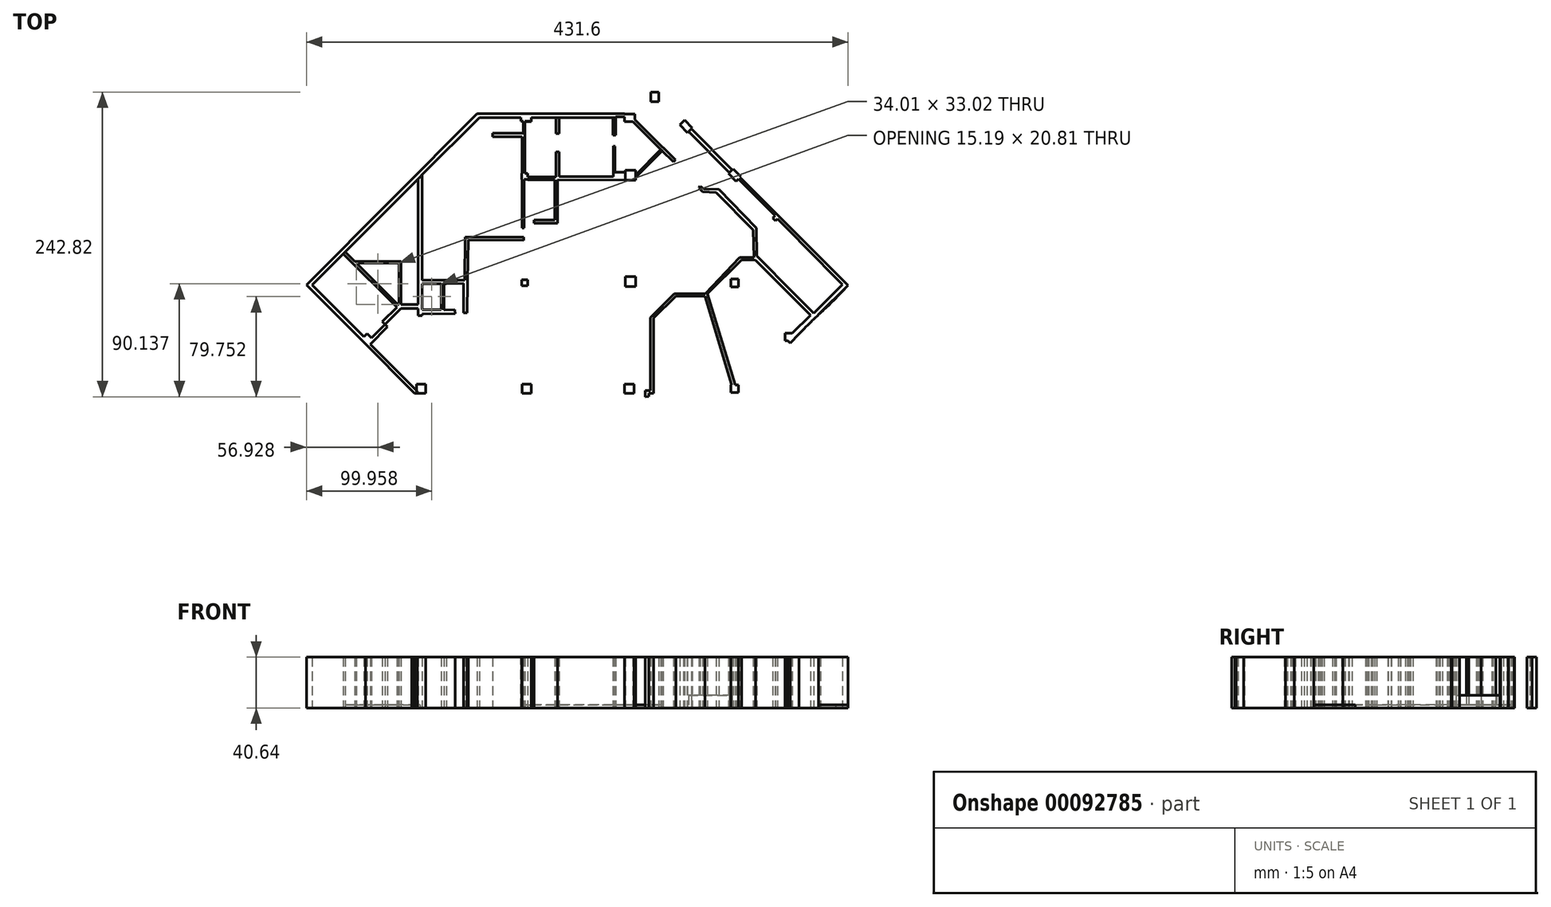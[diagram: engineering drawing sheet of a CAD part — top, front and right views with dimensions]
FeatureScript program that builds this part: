
annotation { "Feature Type Name" : "Feature", "Feature Type Description" : "" }
export const myFeature = defineFeature(function(context is Context, id is Id, definition is map)
    precondition{}
    {
        {
            var Q0;
            Q0=qCreatedBy(makeId("Top.planeOp"),FACE);
            var sketch = newSketch(context, id + "F0", { "sketchPlane" : qUnion([Q0])});
            skFitSpline(sketch, "E0", {"points": [v(215.85, -30.91) * mm, v(202.31, -44.9) * mm, v(186.07, -60.28) * mm, v(172.5, -74.45) * mm]});
            skFitSpline(sketch, "E1", {"points": [v(172.5, -74.45) * mm, v(171.88, -75.1) * mm, v(175.67, -77.18) * mm, v(175.03, -77.82) * mm]});
            skLineSegment(sketch, "E2", {"start": v(-215.85, -30.42) * mm, "end": v(-79.78, 105.85) * mm});
            skLineSegment(sketch, "E3", {"start": v(-79.78, 105.85) * mm, "end": v(46.96, 105.85) * mm});
            skLineSegment(sketch, "E4", {"start": v(46.96, 105.85) * mm, "end": v(58.85, 117.75) * mm});
            skLineSegment(sketch, "E5", {"start": v(58.85, 117.75) * mm, "end": v(58.85, 123.23) * mm});
            skLineSegment(sketch, "E6", {"start": v(58.85, 123.23) * mm, "end": v(65.02, 123.23) * mm});
            skLineSegment(sketch, "E7", {"start": v(65.02, 123.23) * mm, "end": v(65.02, 119.77) * mm});
            skLineSegment(sketch, "E8", {"start": v(65.02, 119.77) * mm, "end": v(84.8, 100) * mm});
            skLineSegment(sketch, "E9", {"start": v(84.8, 100) * mm, "end": v(85.59, 100.78) * mm});
            skLineSegment(sketch, "E10", {"start": v(85.59, 100.78) * mm, "end": v(91.7, 94.67) * mm});
            skLineSegment(sketch, "E11", {"start": v(91.7, 94.67) * mm, "end": v(90.95, 93.92) * mm});
            skLineSegment(sketch, "E12", {"start": v(90.95, 93.92) * mm, "end": v(123.63, 61.24) * mm});
            skLineSegment(sketch, "E13", {"start": v(123.63, 61.24) * mm, "end": v(124.34, 61.95) * mm});
            skLineSegment(sketch, "E14", {"start": v(124.34, 61.95) * mm, "end": v(130.43, 55.86) * mm});
            skLineSegment(sketch, "E15", {"start": v(130.43, 55.86) * mm, "end": v(129.76, 55.18) * mm});
            skLineSegment(sketch, "E16", {"start": v(129.76, 55.18) * mm, "end": v(215.85, -30.91) * mm});
            skLineSegment(sketch, "E17", {"start": v(175.03, -77.82) * mm, "end": v(130.22, -123.23) * mm});
            skLineSegment(sketch, "E18", {"start": v(130.22, -123.23) * mm, "end": v(-126.45, -123.2) * mm});
            skLineSegment(sketch, "E19", {"start": v(-126.45, -123.2) * mm, "end": v(-126.52, -117) * mm});
            skLineSegment(sketch, "E20", {"start": v(-126.52, -117) * mm, "end": v(-129.44, -116.92) * mm});
            skLineSegment(sketch, "E21", {"start": v(-129.44, -116.92) * mm, "end": v(-132.8, -113.69) * mm});
            skLineSegment(sketch, "E22", {"start": v(-132.8, -113.69) * mm, "end": v(-167.08, -79.4) * mm});
            skLineSegment(sketch, "E23", {"start": v(-167.08, -79.4) * mm, "end": v(-168.6, -77.64) * mm});
            skLineSegment(sketch, "E24", {"start": v(-168.6, -77.64) * mm, "end": v(-215.85, -30.42) * mm});
            skLineSegment(sketch, "E25", {"start": v(-126.82, 53.9) * mm, "end": v(-126.8, -46) * mm});
            skLineSegment(sketch, "E26", {"start": v(-126.8, -46) * mm, "end": v(-140.51, -46) * mm});
            skLineSegment(sketch, "E27", {"start": v(-140.51, -46) * mm, "end": v(-140.51, -11.77) * mm});
            skLineSegment(sketch, "E28", {"start": v(-140.51, -11.77) * mm, "end": v(-177.03, -11.77) * mm});
            skLineSegment(sketch, "E29", {"start": v(-177.03, -11.77) * mm, "end": v(-184.78, -4.06) * mm});
            skLineSegment(sketch, "E30", {"start": v(-184.78, -4.06) * mm, "end": v(-186.43, -5.7) * mm});
            skLineSegment(sketch, "E31", {"start": v(-186.43, -5.7) * mm, "end": v(-143.7, -48.36) * mm});
            skLineSegment(sketch, "E32", {"start": v(-143.7, -48.36) * mm, "end": v(-155.43, -59.75) * mm});
            skLineSegment(sketch, "E33", {"start": v(-155.43, -59.75) * mm, "end": v(-153.01, -61.89) * mm});
            skLineSegment(sketch, "E34", {"start": v(-153.01, -61.89) * mm, "end": v(-140.38, -49.21) * mm});
            skLineSegment(sketch, "E35", {"start": v(-140.38, -49.21) * mm, "end": v(-126.8, -49.28) * mm});
            skLineSegment(sketch, "E36", {"start": v(-126.8, -49.28) * mm, "end": v(-126.8, -55.02) * mm});
            skLineSegment(sketch, "E37", {"start": v(-126.8, -55.02) * mm, "end": v(-123.39, -55.02) * mm});
            skLineSegment(sketch, "E38", {"start": v(-123.39, -55.02) * mm, "end": v(-123.39, -53.84) * mm});
            skLineSegment(sketch, "E39", {"start": v(-123.39, -53.84) * mm, "end": v(-97.3, -53.56) * mm});
            skLineSegment(sketch, "E40", {"start": v(-97.3, -53.56) * mm, "end": v(-97.4, -50.34) * mm});
            skLineSegment(sketch, "E41", {"start": v(-97.4, -50.34) * mm, "end": v(-106.13, -50.62) * mm});
            skLineSegment(sketch, "E42", {"start": v(-106.13, -50.62) * mm, "end": v(-106.13, -47.71) * mm});
            skLineSegment(sketch, "E43", {"start": v(-106.13, -47.71) * mm, "end": v(-106.13, -37.32) * mm});
            skLineSegment(sketch, "E44", {"start": v(-106.13, -37.32) * mm, "end": v(-106.13, -29.47) * mm});
            skLineSegment(sketch, "E45", {"start": v(-106.13, -29.47) * mm, "end": v(-104.14, -29.47) * mm});
            skLineSegment(sketch, "E46", {"start": v(-104.14, -29.47) * mm, "end": v(-90.55, -29.32) * mm});
            skLineSegment(sketch, "E47", {"start": v(-90.55, -29.32) * mm, "end": v(-90.46, -52.83) * mm});
            skLineSegment(sketch, "E48", {"start": v(-90.46, -52.83) * mm, "end": v(-87.5, -52.8) * mm});
            skLineSegment(sketch, "E49", {"start": v(-87.5, -52.8) * mm, "end": v(-87.23, -27.68) * mm});
            skLineSegment(sketch, "E50", {"start": v(-87.23, -27.68) * mm, "end": v(-86.84, 5.2) * mm});
            skLineSegment(sketch, "E51", {"start": v(-86.84, 5.2) * mm, "end": v(-42.6, 4.94) * mm});
            skLineSegment(sketch, "E52", {"start": v(-42.6, 4.94) * mm, "end": v(-42.48, 7.54) * mm});
            skLineSegment(sketch, "E53", {"start": v(-42.48, 7.54) * mm, "end": v(-89.25, 7.47) * mm});
            skLineSegment(sketch, "E54", {"start": v(-89.25, 7.47) * mm, "end": v(-89.44, -26.72) * mm});
            skLineSegment(sketch, "E55", {"start": v(-89.44, -26.72) * mm, "end": v(-100.11, -26.77) * mm});
            skLineSegment(sketch, "E56", {"start": v(-100.11, -26.77) * mm, "end": v(-103.15, -26.77) * mm});
            skLineSegment(sketch, "E57", {"start": v(-103.15, -26.77) * mm, "end": v(-123.39, -26.77) * mm});
            skLineSegment(sketch, "E58", {"start": v(-123.39, -26.77) * mm, "end": v(-123.39, 24.46) * mm});
            skLineSegment(sketch, "E59", {"start": v(-123.39, 24.46) * mm, "end": v(-123.4, 57.33) * mm});
            skLineSegment(sketch, "E60", {"start": v(-123.4, 57.33) * mm, "end": v(-126.82, 53.9) * mm});
            skLineSegment(sketch, "E61", {"start": v(-16.97, 102.82) * mm, "end": v(-16.98, 90.17) * mm});
            skLineSegment(sketch, "E62", {"start": v(-16.98, 90.17) * mm, "end": v(-14.46, 90.17) * mm});
            skLineSegment(sketch, "E63", {"start": v(-14.46, 90.17) * mm, "end": v(-14.46, 102.82) * mm});
            skLineSegment(sketch, "E64", {"start": v(-14.46, 102.82) * mm, "end": v(-16.97, 102.82) * mm});
            skFitSpline(sketch, "E65", {"points": [v(-43.9, 14.88) * mm, v(-43.9, 14.88) * mm, v(-42.18, 14.58) * mm, v(-42.18, 14.88) * mm, v(-43.9, 14.88) * mm]});
            skLineSegment(sketch, "E66", {"start": v(66.76, 77.4) * mm, "end": v(46.57, 57.21) * mm});
            skLineSegment(sketch, "E67", {"start": v(46.57, 57.21) * mm, "end": v(46.57, 56.84) * mm});
            skLineSegment(sketch, "E68", {"start": v(46.57, 56.84) * mm, "end": v(46.57, 60.9) * mm});
            skLineSegment(sketch, "E69", {"start": v(46.57, 60.9) * mm, "end": v(38.5, 60.9) * mm});
            skLineSegment(sketch, "E70", {"start": v(38.5, 60.9) * mm, "end": v(38.5, 59.43) * mm});
            skLineSegment(sketch, "E71", {"start": v(38.5, 59.43) * mm, "end": v(30.24, 59.43) * mm});
            skLineSegment(sketch, "E72", {"start": v(30.24, 59.43) * mm, "end": v(30.24, 79.9) * mm});
            skLineSegment(sketch, "E73", {"start": v(30.24, 79.9) * mm, "end": v(28.78, 80.3) * mm});
            skLineSegment(sketch, "E74", {"start": v(28.78, 80.3) * mm, "end": v(28.78, 55.7) * mm});
            skLineSegment(sketch, "E75", {"start": v(28.78, 55.7) * mm, "end": v(27.67, 55.7) * mm});
            skLineSegment(sketch, "E76", {"start": v(27.67, 55.7) * mm, "end": v(-14.36, 55.7) * mm});
            skLineSegment(sketch, "E77", {"start": v(-14.36, 55.7) * mm, "end": v(-14.36, 75.35) * mm});
            skLineSegment(sketch, "E78", {"start": v(-14.36, 75.35) * mm, "end": v(-16.88, 75.35) * mm});
            skLineSegment(sketch, "E79", {"start": v(-16.88, 75.35) * mm, "end": v(-16.88, 55.6) * mm});
            skLineSegment(sketch, "E80", {"start": v(-16.88, 55.6) * mm, "end": v(-39.28, 55.6) * mm});
            skLineSegment(sketch, "E81", {"start": v(-39.28, 55.6) * mm, "end": v(-39.28, 58.34) * mm});
            skLineSegment(sketch, "E82", {"start": v(-39.28, 58.34) * mm, "end": v(-41.58, 58.34) * mm});
            skLineSegment(sketch, "E83", {"start": v(-41.58, 58.34) * mm, "end": v(-41.58, 99.68) * mm});
            skLineSegment(sketch, "E84", {"start": v(-41.58, 99.68) * mm, "end": v(-36.58, 99.68) * mm});
            skLineSegment(sketch, "E85", {"start": v(-36.58, 99.68) * mm, "end": v(-36.58, 102.83) * mm});
            skLineSegment(sketch, "E86", {"start": v(-36.58, 102.83) * mm, "end": v(-44.9, 102.83) * mm});
            skLineSegment(sketch, "E87", {"start": v(-44.9, 102.83) * mm, "end": v(-44.98, 99.68) * mm});
            skLineSegment(sketch, "E88", {"start": v(-44.98, 99.68) * mm, "end": v(-42.68, 99.68) * mm});
            skLineSegment(sketch, "E89", {"start": v(-42.68, 99.68) * mm, "end": v(-42.68, 90.28) * mm});
            skLineSegment(sketch, "E90", {"start": v(-42.68, 90.28) * mm, "end": v(-67.28, 90.28) * mm});
            skLineSegment(sketch, "E91", {"start": v(-67.28, 90.28) * mm, "end": v(-67.28, 87.66) * mm});
            skLineSegment(sketch, "E92", {"start": v(-67.28, 87.66) * mm, "end": v(-43.8, 87.66) * mm});
            skLineSegment(sketch, "E93", {"start": v(-43.8, 87.66) * mm, "end": v(-43.8, 58.34) * mm});
            skLineSegment(sketch, "E94", {"start": v(-43.8, 58.34) * mm, "end": v(-44.13, 58.34) * mm});
            skLineSegment(sketch, "E95", {"start": v(-44.13, 58.34) * mm, "end": v(-44.13, 53.49) * mm});
            skLineSegment(sketch, "E96", {"start": v(-44.13, 53.49) * mm, "end": v(-43.9, 53.49) * mm});
            skLineSegment(sketch, "E97", {"start": v(-43.9, 53.49) * mm, "end": v(-43.9, 14.88) * mm});
            skFitSpline(sketch, "E98", {"points": [v(46.56, 55.03) * mm, v(47.71, 55.85) * mm, v(67.81, 76.29) * mm, v(67.81, 76.29) * mm, v(46.56, 55.03) * mm]});
            skLineSegment(sketch, "E99", {"start": v(-42.18, 14.88) * mm, "end": v(-42.18, 53.49) * mm});
            skLineSegment(sketch, "E100", {"start": v(-42.18, 53.49) * mm, "end": v(-39.46, 53.49) * mm});
            skLineSegment(sketch, "E101", {"start": v(-39.46, 53.49) * mm, "end": v(-39.46, 53.29) * mm});
            skLineSegment(sketch, "E102", {"start": v(-39.46, 53.29) * mm, "end": v(-17.89, 53.29) * mm});
            skLineSegment(sketch, "E103", {"start": v(-17.89, 53.29) * mm, "end": v(-17.89, 21.13) * mm});
            skLineSegment(sketch, "E104", {"start": v(-17.89, 21.13) * mm, "end": v(-34.32, 21.13) * mm});
            skLineSegment(sketch, "E105", {"start": v(-34.32, 21.13) * mm, "end": v(-34.32, 18.81) * mm});
            skLineSegment(sketch, "E106", {"start": v(-34.32, 18.81) * mm, "end": v(-15.67, 18.81) * mm});
            skLineSegment(sketch, "E107", {"start": v(-15.67, 18.81) * mm, "end": v(-15.67, 53.08) * mm});
            skLineSegment(sketch, "E108", {"start": v(-15.67, 53.08) * mm, "end": v(38.5, 53.08) * mm});
            skLineSegment(sketch, "E109", {"start": v(38.5, 53.08) * mm, "end": v(38.5, 52.83) * mm});
            skLineSegment(sketch, "E110", {"start": v(38.5, 52.83) * mm, "end": v(46.56, 52.83) * mm});
            skLineSegment(sketch, "E111", {"start": v(46.56, 52.83) * mm, "end": v(46.56, 55.03) * mm});
            skLineSegment(sketch, "E112", {"start": v(67.81, 76.29) * mm, "end": v(66.76, 77.4) * mm});
            skLineSegment(sketch, "E113", {"start": v(76.66, 67.44) * mm, "end": v(78.4, 69.18) * mm});
            skLineSegment(sketch, "E114", {"start": v(78.4, 69.18) * mm, "end": v(68.46, 79.11) * mm});
            skLineSegment(sketch, "E115", {"start": v(68.46, 79.11) * mm, "end": v(68.37, 79.01) * mm});
            skLineSegment(sketch, "E116", {"start": v(68.37, 79.01) * mm, "end": v(46.1, 101.07) * mm});
            skLineSegment(sketch, "E117", {"start": v(46.1, 101.07) * mm, "end": v(46.1, 105.52) * mm});
            skLineSegment(sketch, "E118", {"start": v(46.1, 105.52) * mm, "end": v(37.73, 105.52) * mm});
            skLineSegment(sketch, "E119", {"start": v(37.73, 105.52) * mm, "end": v(37.7, 105.8) * mm});
            skLineSegment(sketch, "E120", {"start": v(37.7, 105.8) * mm, "end": v(-79.76, 105.8) * mm});
            skLineSegment(sketch, "E121", {"start": v(-79.76, 105.8) * mm, "end": v(-215.75, -30.47) * mm});
            skLineSegment(sketch, "E122", {"start": v(-215.75, -30.47) * mm, "end": v(-168.57, -77.66) * mm});
            skLineSegment(sketch, "E123", {"start": v(-168.57, -77.66) * mm, "end": v(-168.48, -77.57) * mm});
            skLineSegment(sketch, "E124", {"start": v(-168.48, -77.57) * mm, "end": v(-129.43, -117.04) * mm});
            skLineSegment(sketch, "E125", {"start": v(-129.43, -117.04) * mm, "end": v(-127.3, -117.04) * mm});
            skLineSegment(sketch, "E126", {"start": v(-127.3, -117.04) * mm, "end": v(-127.3, -115.33) * mm});
            skLineSegment(sketch, "E127", {"start": v(-127.3, -115.33) * mm, "end": v(-164.85, -77.78) * mm});
            skLineSegment(sketch, "E128", {"start": v(-164.85, -77.78) * mm, "end": v(-151.03, -63.95) * mm});
            skLineSegment(sketch, "E129", {"start": v(-151.03, -63.95) * mm, "end": v(-153.09, -61.88) * mm});
            skLineSegment(sketch, "E130", {"start": v(-153.09, -61.88) * mm, "end": v(-163.87, -72.66) * mm});
            skLineSegment(sketch, "E131", {"start": v(-163.87, -72.66) * mm, "end": v(-167.29, -69.24) * mm});
            skLineSegment(sketch, "E132", {"start": v(-167.29, -69.24) * mm, "end": v(-169.86, -71.8) * mm});
            skLineSegment(sketch, "E133", {"start": v(-169.86, -71.8) * mm, "end": v(-211.2, -30.47) * mm});
            skLineSegment(sketch, "E134", {"start": v(-211.2, -30.47) * mm, "end": v(-77.91, 102.8) * mm});
            skLineSegment(sketch, "E135", {"start": v(-77.91, 102.8) * mm, "end": v(-56.96, 102.8) * mm});
            skLineSegment(sketch, "E136", {"start": v(-56.96, 102.8) * mm, "end": v(-53.35, 102.8) * mm});
            skLineSegment(sketch, "E137", {"start": v(-53.35, 102.8) * mm, "end": v(28.56, 102.8) * mm});
            skLineSegment(sketch, "E138", {"start": v(28.56, 102.8) * mm, "end": v(30.9, 102.84) * mm});
            skLineSegment(sketch, "E139", {"start": v(30.9, 102.84) * mm, "end": v(30.91, 103.52) * mm});
            skLineSegment(sketch, "E140", {"start": v(30.91, 103.52) * mm, "end": v(37.7, 103.52) * mm});
            skLineSegment(sketch, "E141", {"start": v(37.7, 103.52) * mm, "end": v(37.7, 99.68) * mm});
            skLineSegment(sketch, "E142", {"start": v(37.7, 99.68) * mm, "end": v(44.47, 99.68) * mm});
            skLineSegment(sketch, "E143", {"start": v(44.47, 99.68) * mm, "end": v(76.66, 67.44) * mm});
            skLineSegment(sketch, "E144", {"start": v(28.57, 102.8) * mm, "end": v(28.56, 88.7) * mm});
            skLineSegment(sketch, "E145", {"start": v(28.56, 88.7) * mm, "end": v(30.91, 88.76) * mm});
            skLineSegment(sketch, "E146", {"start": v(30.91, 88.76) * mm, "end": v(30.88, 102.86) * mm});
            skLineSegment(sketch, "E147", {"start": v(30.88, 102.86) * mm, "end": v(28.57, 102.8) * mm});
            skLineSegment(sketch, "E148", {"start": v(-175.83, -12.98) * mm, "end": v(-141.82, -12.98) * mm});
            skLineSegment(sketch, "E149", {"start": v(-141.82, -12.98) * mm, "end": v(-141.82, -46) * mm});
            skLineSegment(sketch, "E150", {"start": v(-141.82, -46) * mm, "end": v(-142.77, -46) * mm});
            skLineSegment(sketch, "E151", {"start": v(-142.77, -46) * mm, "end": v(-175.83, -12.98) * mm});
            skLineSegment(sketch, "E152", {"start": v(-123.39, -29.47) * mm, "end": v(-108.2, -29.47) * mm});
            skLineSegment(sketch, "E153", {"start": v(-108.2, -29.47) * mm, "end": v(-108.2, -36.4) * mm});
            skLineSegment(sketch, "E154", {"start": v(-108.2, -36.4) * mm, "end": v(-108.41, -47.51) * mm});
            skLineSegment(sketch, "E155", {"start": v(-108.41, -47.51) * mm, "end": v(-108.38, -50.28) * mm});
            skLineSegment(sketch, "E156", {"start": v(-108.38, -50.28) * mm, "end": v(-123.39, -50.28) * mm});
            skLineSegment(sketch, "E157", {"start": v(-123.39, -50.28) * mm, "end": v(-123.39, -29.47) * mm});
            skLineSegment(sketch, "E158", {"start": v(-44.13, -26.48) * mm, "end": v(-39.28, -26.48) * mm});
            skLineSegment(sketch, "E159", {"start": v(-39.28, -26.48) * mm, "end": v(-39.28, -31.32) * mm});
            skLineSegment(sketch, "E160", {"start": v(-39.28, -31.32) * mm, "end": v(-44.13, -31.32) * mm});
            skLineSegment(sketch, "E161", {"start": v(-44.13, -31.32) * mm, "end": v(-44.13, -26.48) * mm});
            skLineSegment(sketch, "E162", {"start": v(124.35, 62) * mm, "end": v(120.57, 58.23) * mm});
            skLineSegment(sketch, "E163", {"start": v(120.57, 58.23) * mm, "end": v(126.7, 52.1) * mm});
            skLineSegment(sketch, "E164", {"start": v(126.7, 52.1) * mm, "end": v(128.56, 53.96) * mm});
            skLineSegment(sketch, "E165", {"start": v(128.56, 53.96) * mm, "end": v(157.7, 24.77) * mm});
            skLineSegment(sketch, "E166", {"start": v(157.7, 24.77) * mm, "end": v(155.8, 22.87) * mm});
            skLineSegment(sketch, "E167", {"start": v(155.8, 22.87) * mm, "end": v(157.96, 20.48) * mm});
            skLineSegment(sketch, "E168", {"start": v(157.96, 20.48) * mm, "end": v(159.59, 22.13) * mm});
            skLineSegment(sketch, "E169", {"start": v(159.59, 22.13) * mm, "end": v(193.9, -12.57) * mm});
            skLineSegment(sketch, "E170", {"start": v(193.9, -12.57) * mm, "end": v(198.22, -16.85) * mm});
            skLineSegment(sketch, "E171", {"start": v(198.22, -16.85) * mm, "end": v(211.45, -30.18) * mm});
            skLineSegment(sketch, "E172", {"start": v(211.45, -30.18) * mm, "end": v(188.53, -53.1) * mm});
            skLineSegment(sketch, "E173", {"start": v(188.53, -53.1) * mm, "end": v(172.67, -37.2) * mm});
            skLineSegment(sketch, "E174", {"start": v(172.67, -37.2) * mm, "end": v(143.11, -7.23) * mm});
            skLineSegment(sketch, "E175", {"start": v(143.11, -7.23) * mm, "end": v(142.78, 14.73) * mm});
            skLineSegment(sketch, "E176", {"start": v(142.78, 14.73) * mm, "end": v(113, 45.5) * mm});
            skLineSegment(sketch, "E177", {"start": v(113, 45.5) * mm, "end": v(100.86, 45.83) * mm});
            skLineSegment(sketch, "E178", {"start": v(100.86, 45.83) * mm, "end": v(98.06, 48.17) * mm});
            skLineSegment(sketch, "E179", {"start": v(98.06, 48.17) * mm, "end": v(97.12, 46.46) * mm});
            skLineSegment(sketch, "E180", {"start": v(97.12, 46.46) * mm, "end": v(99.87, 43.74) * mm});
            skLineSegment(sketch, "E181", {"start": v(99.87, 43.74) * mm, "end": v(110.89, 43.22) * mm});
            skLineSegment(sketch, "E182", {"start": v(110.89, 43.22) * mm, "end": v(140.17, 13.18) * mm});
            skLineSegment(sketch, "E183", {"start": v(140.17, 13.18) * mm, "end": v(141.01, -8.52) * mm});
            skLineSegment(sketch, "E184", {"start": v(141.01, -8.52) * mm, "end": v(129.6, -8.57) * mm});
            skLineSegment(sketch, "E185", {"start": v(129.6, -8.57) * mm, "end": v(102.25, -37.52) * mm});
            skLineSegment(sketch, "E186", {"start": v(102.25, -37.52) * mm, "end": v(87.7, -37.53) * mm});
            skLineSegment(sketch, "E187", {"start": v(87.7, -37.53) * mm, "end": v(87.7, -37.54) * mm});
            skLineSegment(sketch, "E188", {"start": v(87.7, -37.54) * mm, "end": v(77.36, -37.54) * mm});
            skLineSegment(sketch, "E189", {"start": v(77.36, -37.54) * mm, "end": v(58.26, -56.63) * mm});
            skLineSegment(sketch, "E190", {"start": v(58.26, -56.63) * mm, "end": v(58.26, -114.64) * mm});
            skLineSegment(sketch, "E191", {"start": v(58.26, -114.64) * mm, "end": v(54.43, -114.64) * mm});
            skLineSegment(sketch, "E192", {"start": v(54.43, -114.64) * mm, "end": v(54.43, -119.63) * mm});
            skLineSegment(sketch, "E193", {"start": v(54.43, -119.63) * mm, "end": v(57, -119.57) * mm});
            skLineSegment(sketch, "E194", {"start": v(57, -119.57) * mm, "end": v(57, -117.06) * mm});
            skLineSegment(sketch, "E195", {"start": v(57, -117.06) * mm, "end": v(61.04, -117.06) * mm});
            skLineSegment(sketch, "E196", {"start": v(61.04, -117.06) * mm, "end": v(61.04, -56.89) * mm});
            skLineSegment(sketch, "E197", {"start": v(61.04, -56.89) * mm, "end": v(78.57, -39.34) * mm});
            skLineSegment(sketch, "E198", {"start": v(78.57, -39.34) * mm, "end": v(87.7, -39.34) * mm});
            skLineSegment(sketch, "E199", {"start": v(87.7, -39.34) * mm, "end": v(87.85, -39.34) * mm});
            skLineSegment(sketch, "E200", {"start": v(87.85, -39.34) * mm, "end": v(101.82, -39.34) * mm});
            skLineSegment(sketch, "E201", {"start": v(101.82, -39.34) * mm, "end": v(123.22, -110.16) * mm});
            skLineSegment(sketch, "E202", {"start": v(123.22, -110.16) * mm, "end": v(122.45, -110.16) * mm});
            skLineSegment(sketch, "E203", {"start": v(122.45, -110.16) * mm, "end": v(122.45, -116.28) * mm});
            skLineSegment(sketch, "E204", {"start": v(122.45, -116.28) * mm, "end": v(128.44, -116.28) * mm});
            skLineSegment(sketch, "E205", {"start": v(128.44, -116.28) * mm, "end": v(128.44, -110.16) * mm});
            skLineSegment(sketch, "E206", {"start": v(128.44, -110.16) * mm, "end": v(125.86, -110.16) * mm});
            skLineSegment(sketch, "E207", {"start": v(125.86, -110.16) * mm, "end": v(103.88, -37.68) * mm});
            skLineSegment(sketch, "E208", {"start": v(103.88, -37.68) * mm, "end": v(131.24, -10.5) * mm});
            skLineSegment(sketch, "E209", {"start": v(131.24, -10.5) * mm, "end": v(142.19, -10.81) * mm});
            skLineSegment(sketch, "E210", {"start": v(142.19, -10.81) * mm, "end": v(186.15, -54.84) * mm});
            skLineSegment(sketch, "E211", {"start": v(186.15, -54.84) * mm, "end": v(166.45, -73.8) * mm});
            skLineSegment(sketch, "E212", {"start": v(166.45, -73.8) * mm, "end": v(169.77, -76.83) * mm});
            skLineSegment(sketch, "E213", {"start": v(169.77, -76.83) * mm, "end": v(215.8, -30.93) * mm});
            skLineSegment(sketch, "E214", {"start": v(215.8, -30.93) * mm, "end": v(159.12, 26.2) * mm});
            skLineSegment(sketch, "E215", {"start": v(159.12, 26.2) * mm, "end": v(159.1, 26.18) * mm});
            skLineSegment(sketch, "E216", {"start": v(159.1, 26.18) * mm, "end": v(129.96, 55.36) * mm});
            skLineSegment(sketch, "E217", {"start": v(129.96, 55.36) * mm, "end": v(130.5, 55.88) * mm});
            skLineSegment(sketch, "E218", {"start": v(130.5, 55.88) * mm, "end": v(124.35, 62) * mm});
            skLineSegment(sketch, "E219", {"start": v(38.5, 60.9) * mm, "end": v(46.56, 60.9) * mm});
            skLineSegment(sketch, "E220", {"start": v(46.56, 60.9) * mm, "end": v(46.56, 52.83) * mm});
            skLineSegment(sketch, "E221", {"start": v(46.56, 52.83) * mm, "end": v(38.5, 52.83) * mm});
            skLineSegment(sketch, "E222", {"start": v(38.5, 52.83) * mm, "end": v(38.5, 60.9) * mm});
            skLineSegment(sketch, "E223", {"start": v(38.5, -23.77) * mm, "end": v(46.56, -23.77) * mm});
            skLineSegment(sketch, "E224", {"start": v(46.56, -23.77) * mm, "end": v(46.56, -31.83) * mm});
            skLineSegment(sketch, "E225", {"start": v(46.56, -31.83) * mm, "end": v(38.5, -31.83) * mm});
            skLineSegment(sketch, "E226", {"start": v(38.5, -31.83) * mm, "end": v(38.5, -23.77) * mm});
            skLineSegment(sketch, "E227", {"start": v(85.58, 100.79) * mm, "end": v(91.72, 94.65) * mm});
            skLineSegment(sketch, "E228", {"start": v(91.72, 94.65) * mm, "end": v(87.93, 90.86) * mm});
            skLineSegment(sketch, "E229", {"start": v(87.93, 90.86) * mm, "end": v(81.8, 97) * mm});
            skLineSegment(sketch, "E230", {"start": v(81.8, 97) * mm, "end": v(85.58, 100.79) * mm});
            skLineSegment(sketch, "E231", {"start": v(58.79, 123.2) * mm, "end": v(65.06, 123.2) * mm});
            skLineSegment(sketch, "E232", {"start": v(65.06, 123.2) * mm, "end": v(65.06, 115.5) * mm});
            skLineSegment(sketch, "E233", {"start": v(65.06, 115.5) * mm, "end": v(58.79, 115.5) * mm});
            skLineSegment(sketch, "E234", {"start": v(58.79, 115.5) * mm, "end": v(58.79, 123.2) * mm});
            skLineSegment(sketch, "E235", {"start": v(-43.9, -109.5) * mm, "end": v(-36.5, -109.5) * mm});
            skLineSegment(sketch, "E236", {"start": v(-36.5, -109.5) * mm, "end": v(-36.5, -116.9) * mm});
            skLineSegment(sketch, "E237", {"start": v(-36.5, -116.9) * mm, "end": v(-43.9, -116.9) * mm});
            skLineSegment(sketch, "E238", {"start": v(-43.9, -116.9) * mm, "end": v(-43.9, -109.5) * mm});
            skLineSegment(sketch, "E239", {"start": v(37.92, -109.5) * mm, "end": v(45.33, -109.5) * mm});
            skLineSegment(sketch, "E240", {"start": v(45.33, -109.5) * mm, "end": v(45.33, -116.9) * mm});
            skLineSegment(sketch, "E241", {"start": v(45.33, -116.9) * mm, "end": v(37.92, -116.9) * mm});
            skLineSegment(sketch, "E242", {"start": v(37.92, -116.9) * mm, "end": v(37.92, -109.5) * mm});
            skLineSegment(sketch, "E243", {"start": v(-128, -109.5) * mm, "end": v(-120.6, -109.5) * mm});
            skLineSegment(sketch, "E244", {"start": v(-120.6, -109.5) * mm, "end": v(-120.6, -116.9) * mm});
            skLineSegment(sketch, "E245", {"start": v(-120.6, -116.9) * mm, "end": v(-128, -116.9) * mm});
            skLineSegment(sketch, "E246", {"start": v(-128, -116.9) * mm, "end": v(-128, -109.5) * mm});
            skLineSegment(sketch, "E247", {"start": v(122.45, -25.89) * mm, "end": v(128.43, -25.89) * mm});
            skLineSegment(sketch, "E248", {"start": v(128.43, -25.89) * mm, "end": v(128.43, -32.02) * mm});
            skLineSegment(sketch, "E249", {"start": v(128.43, -32.02) * mm, "end": v(122.45, -32.02) * mm});
            skLineSegment(sketch, "E250", {"start": v(122.45, -32.02) * mm, "end": v(122.45, -25.89) * mm});
            skLineSegment(sketch, "E251", {"start": v(165.64, -68.94) * mm, "end": v(171.62, -68.94) * mm});
            skLineSegment(sketch, "E252", {"start": v(171.62, -68.94) * mm, "end": v(171.62, -75.07) * mm});
            skLineSegment(sketch, "E253", {"start": v(171.62, -75.07) * mm, "end": v(165.64, -75.07) * mm});
            skLineSegment(sketch, "E254", {"start": v(165.64, -75.07) * mm, "end": v(165.64, -68.94) * mm});
            skLineSegment(sketch, "E255", {"start": v(123.59, 61.28) * mm, "end": v(90.98, 93.88) * mm});
            skLineSegment(sketch, "E256", {"start": v(90.98, 93.88) * mm, "end": v(88.72, 91.62) * mm});
            skLineSegment(sketch, "E257", {"start": v(88.72, 91.62) * mm, "end": v(121.33, 59) * mm});
            skLineSegment(sketch, "E258", {"start": v(121.33, 59) * mm, "end": v(123.59, 61.28) * mm});
            skSolve(sketch);
        }
        {
            var Q0;
            {var subQ18=sQuery(id+"F0.wireOp",EDGE,"E30");Q0=makeQuery(id+"F0.imprint","IMPRINT",FACE,{"disambiguationData":[TD([[makeQuery(id+"F0.imprint","IMPRINT",EDGE,{"derivedFrom":subQ18}),-1.0]])]});}
            var Q1;
            {var subQ5=sQuery(id+"F0.wireOp",EDGE,"E25");Q1=makeQuery(id+"F0.imprint","IMPRINT",FACE,{"disambiguationData":[TD([[makeQuery(id+"F0.imprint","IMPRINT",EDGE,{"derivedFrom":subQ5}),1.0]])]});}
            var Q2;
            {var subQ0=sQuery(id+"F0.wireOp",EDGE,"E13");Q2=makeQuery(id+"F0.imprint","IMPRINT",FACE,{"disambiguationData":[TD([[makeQuery(id+"F0.imprint","IMPRINT",EDGE,{"derivedFrom":subQ0}),-1.0]])]});}
            var Q3;
            {var subQ1=sQuery(id+"F0.wireOp",EDGE,"E9");Q3=makeQuery(id+"F0.imprint","IMPRINT",FACE,{"disambiguationData":[TD([[makeQuery(id+"F0.imprint","IMPRINT",EDGE,{"derivedFrom":subQ1}),-1.0]])]});}
            var Q4;
            {var subQ6=sQuery(id+"F0.wireOp",EDGE,"E233");Q4=makeQuery(id+"F0.imprint","IMPRINT",FACE,{"disambiguationData":[TD([[makeQuery(id+"F0.imprint","IMPRINT",EDGE,{"derivedFrom":subQ6}),-1.0]])]});}
            var Q5;
            Q5=makeQuery(id+"F0.imprint","IMPRINT",FACE,{"disambiguationData":[TD([[makeQuery(id+"F0.imprint","IMPRINT",EDGE,{"derivedFrom":sQuery(id+"F0.wireOp",EDGE,"E219")}),-1.0]])]});
            var Q6;
            Q6=makeQuery(id+"F0.imprint","IMPRINT",FACE,{"disambiguationData":[TD([[makeQuery(id+"F0.imprint","IMPRINT",EDGE,{"derivedFrom":sQuery(id+"F0.wireOp",EDGE,"E158")}),-1.0]])]});
            var Q7;
            Q7=makeQuery(id+"F0.imprint","IMPRINT",FACE,{"disambiguationData":[TD([[makeQuery(id+"F0.imprint","IMPRINT",EDGE,{"derivedFrom":sQuery(id+"F0.wireOp",EDGE,"E223")}),-1.0]])]});
            var Q8;
            Q8=makeQuery(id+"F0.imprint","IMPRINT",FACE,{"disambiguationData":[TD([[makeQuery(id+"F0.imprint","IMPRINT",EDGE,{"derivedFrom":sQuery(id+"F0.wireOp",EDGE,"E247")}),-1.0]])]});
            var Q9;
            {var subQ0=sQuery(id+"F0.wireOp",EDGE,"E254");Q9=makeQuery(id+"F0.imprint","IMPRINT",FACE,{"disambiguationData":[TD([[makeQuery(id+"F0.imprint","IMPRINT",EDGE,{"derivedFrom":subQ0}),-1.0]])]});}
            var Q10;
            {var subQ3=sQuery(id+"F0.wireOp",EDGE,"E211");var subQ9=sQuery(id+"F0.wireOp",EDGE,"E212");var subQ10=makeQuery(id+"F0.imprint","INTERSECT",VERTEX,{"derivedFrom":[subQ3,subQ9]});Q10=makeQuery(id+"F0.imprint","IMPRINT",FACE,{"disambiguationData":[TD([[makeQuery(id+"F0.imprint","IMPRINT",EDGE,{"disambiguationData":[TD([[subQ10,1.0]])],"derivedFrom":subQ3}),1.0]])]});}
            var Q11;
            {var subQ0=sQuery(id+"F0.wireOp",EDGE,"E213");var subQ1=sQuery(id+"F0.wireOp",EDGE,"E212");var subQ2=makeQuery(id+"F0.imprint","INTERSECT",VERTEX,{"derivedFrom":[subQ1,subQ0]});Q11=makeQuery(id+"F0.imprint","IMPRINT",FACE,{"disambiguationData":[TD([[makeQuery(id+"F0.imprint","IMPRINT",EDGE,{"disambiguationData":[TD([[subQ2,1.0]])],"derivedFrom":subQ1}),1.0]])]});}
            var Q12;
            Q12=makeQuery(id+"F0.imprint","IMPRINT",FACE,{"disambiguationData":[TD([[makeQuery(id+"F0.imprint","IMPRINT",EDGE,{"derivedFrom":sQuery(id+"F0.wireOp",EDGE,"E239")}),-1.0]])]});
            var Q13;
            Q13=makeQuery(id+"F0.imprint","IMPRINT",FACE,{"disambiguationData":[TD([[makeQuery(id+"F0.imprint","IMPRINT",EDGE,{"derivedFrom":sQuery(id+"F0.wireOp",EDGE,"E235")}),-1.0]])]});
            var Q14;
            {var subQ6=sQuery(id+"F0.wireOp",EDGE,"E243");Q14=makeQuery(id+"F0.imprint","IMPRINT",FACE,{"disambiguationData":[TD([[makeQuery(id+"F0.imprint","IMPRINT",EDGE,{"derivedFrom":subQ6}),-1.0]])]});}
            var Q15;
            {var subQ0=sQuery(id+"F0.wireOp",EDGE,"E62");Q15=makeQuery(id+"F0.imprint","IMPRINT",FACE,{"disambiguationData":[TD([[makeQuery(id+"F0.imprint","IMPRINT",EDGE,{"derivedFrom":subQ0}),1.0]])]});}
            var Q16;
            {var subQ6=sQuery(id+"F0.wireOp",EDGE,"E144");Q16=makeQuery(id+"F0.imprint","IMPRINT",FACE,{"disambiguationData":[TD([[makeQuery(id+"F0.imprint","IMPRINT",EDGE,{"derivedFrom":subQ6}),1.0]])]});}
            extrude(context, id + "F1", {"entities" : qUnion([Q0, Q1, Q2, Q3, Q4, Q5, Q6, Q7, Q8, Q9, Q10, Q11, Q12, Q13, Q14, Q15, Q16]), "depth" : 40.64 * mm});
        }
        {
            var Q0;
            Q0=qCreatedBy(makeId("Top.planeOp"),FACE);
            var sketch = newSketch(context, id + "F2", { "sketchPlane" : qUnion([Q0])});
            skLineSegment(sketch, "E259", {"start": v(-36.65, 103.38) * mm, "end": v(-44.76, 103.38) * mm});
            skLineSegment(sketch, "E260", {"start": v(-44.76, 103.38) * mm, "end": v(-44.76, 99.82) * mm});
            skLineSegment(sketch, "E261", {"start": v(-44.76, 99.82) * mm, "end": v(-42.78, 99.82) * mm});
            skLineSegment(sketch, "E262", {"start": v(-42.78, 99.82) * mm, "end": v(-42.78, 90.33) * mm});
            skLineSegment(sketch, "E263", {"start": v(-42.78, 90.33) * mm, "end": v(-67.44, 90.33) * mm});
            skLineSegment(sketch, "E264", {"start": v(-67.44, 90.33) * mm, "end": v(-67.44, 87.63) * mm});
            skLineSegment(sketch, "E265", {"start": v(-67.44, 87.63) * mm, "end": v(-43.84, 87.63) * mm});
            skLineSegment(sketch, "E266", {"start": v(-43.84, 87.63) * mm, "end": v(-43.84, 58.4) * mm});
            skLineSegment(sketch, "E267", {"start": v(-43.84, 58.4) * mm, "end": v(-44.12, 58.4) * mm});
            skLineSegment(sketch, "E268", {"start": v(-44.12, 58.4) * mm, "end": v(-44.12, 53.5) * mm});
            skLineSegment(sketch, "E269", {"start": v(-44.12, 53.5) * mm, "end": v(-43.87, 53.5) * mm});
            skLineSegment(sketch, "E270", {"start": v(-43.87, 53.5) * mm, "end": v(-43.87, 14.93) * mm});
            skLineSegment(sketch, "E271", {"start": v(-43.87, 14.93) * mm, "end": v(-42.25, 14.93) * mm});
            skLineSegment(sketch, "E272", {"start": v(-42.25, 14.93) * mm, "end": v(-42.25, 53.5) * mm});
            skLineSegment(sketch, "E273", {"start": v(-42.25, 53.5) * mm, "end": v(-39.47, 53.5) * mm});
            skLineSegment(sketch, "E274", {"start": v(-39.47, 53.5) * mm, "end": v(-39.47, 53.26) * mm});
            skLineSegment(sketch, "E275", {"start": v(-39.47, 53.26) * mm, "end": v(-17.87, 53.26) * mm});
            skLineSegment(sketch, "E276", {"start": v(-17.87, 53.26) * mm, "end": v(-17.87, 21.1) * mm});
            skLineSegment(sketch, "E277", {"start": v(-17.87, 21.1) * mm, "end": v(-34.32, 21.1) * mm});
            skLineSegment(sketch, "E278", {"start": v(-34.32, 21.1) * mm, "end": v(-34.32, 18.69) * mm});
            skLineSegment(sketch, "E279", {"start": v(-34.32, 18.69) * mm, "end": v(-15.49, 18.69) * mm});
            skLineSegment(sketch, "E280", {"start": v(-15.49, 18.69) * mm, "end": v(-15.49, 53.26) * mm});
            skLineSegment(sketch, "E281", {"start": v(-15.49, 53.26) * mm, "end": v(38.47, 53) * mm});
            skLineSegment(sketch, "E282", {"start": v(38.47, 53) * mm, "end": v(38.47, 59.44) * mm});
            skLineSegment(sketch, "E283", {"start": v(38.47, 59.44) * mm, "end": v(30.2, 59.44) * mm});
            skLineSegment(sketch, "E284", {"start": v(30.2, 59.44) * mm, "end": v(30.2, 79.97) * mm});
            skLineSegment(sketch, "E285", {"start": v(30.2, 79.97) * mm, "end": v(28.76, 80.32) * mm});
            skLineSegment(sketch, "E286", {"start": v(28.76, 80.32) * mm, "end": v(28.76, 55.72) * mm});
            skLineSegment(sketch, "E287", {"start": v(28.76, 55.72) * mm, "end": v(-14.32, 55.72) * mm});
            skLineSegment(sketch, "E288", {"start": v(-14.32, 55.72) * mm, "end": v(-14.32, 75.33) * mm});
            skLineSegment(sketch, "E289", {"start": v(-14.32, 75.33) * mm, "end": v(-16.95, 75.33) * mm});
            skLineSegment(sketch, "E290", {"start": v(-16.95, 75.33) * mm, "end": v(-16.95, 55.6) * mm});
            skLineSegment(sketch, "E291", {"start": v(-16.95, 55.6) * mm, "end": v(-39.33, 55.6) * mm});
            skLineSegment(sketch, "E292", {"start": v(-39.33, 55.6) * mm, "end": v(-39.33, 58.42) * mm});
            skLineSegment(sketch, "E293", {"start": v(-39.33, 58.42) * mm, "end": v(-41.58, 58.42) * mm});
            skLineSegment(sketch, "E294", {"start": v(-41.58, 58.42) * mm, "end": v(-41.58, 99.83) * mm});
            skLineSegment(sketch, "E295", {"start": v(-41.58, 99.83) * mm, "end": v(-36.62, 99.83) * mm});
            skLineSegment(sketch, "E296", {"start": v(-36.62, 99.83) * mm, "end": v(-36.65, 103.38) * mm});
            skSolve(sketch);
        }
        {
            var Q0;
            Q0=makeQuery(id+"F2.imprint","IMPRINT",FACE,{"disambiguationData":[TD([[makeQuery(id+"F2.imprint","IMPRINT",EDGE,{"derivedFrom":sQuery(id+"F2.wireOp",EDGE,"E259")}),1.0]])]});
            extrude(context, id + "F3", {"entities" : qUnion([Q0]), "operationType" : NewBodyOperationType.ADD, "depth" : 40.64 * mm});
        }
        {
            var Q0;
            {var subQ40=sQuery(id+"F0.wireOp",EDGE,"E0");Q0=makeQuery(id+"F0.imprint","IMPRINT",FACE,{"disambiguationData":[TD([[makeQuery(id+"F0.imprint","IMPRINT",EDGE,{"derivedFrom":subQ40}),-1.0]])]});}
            var Q1;
            {var subQ0=sQuery(id+"F0.wireOp",EDGE,"E25");Q1=makeQuery(id+"F0.imprint","IMPRINT",FACE,{"disambiguationData":[TD([[makeQuery(id+"F0.imprint","IMPRINT",EDGE,{"derivedFrom":subQ0}),-1.0]])]});}
            var Q2;
            Q2=makeQuery(id+"F0.imprint","IMPRINT",FACE,{"disambiguationData":[TD([[makeQuery(id+"F0.imprint","IMPRINT",EDGE,{"derivedFrom":sQuery(id+"F0.wireOp",EDGE,"E148")}),-1.0]])]});
            var Q3;
            {var subQ9=sQuery(id+"F0.wireOp",EDGE,"E62");Q3=makeQuery(id+"F0.imprint","IMPRINT",FACE,{"disambiguationData":[TD([[makeQuery(id+"F0.imprint","IMPRINT",EDGE,{"derivedFrom":subQ9}),-1.0]])]});}
            extrude(context, id + "F4", {"entities" : qUnion([Q0, Q1, Q2, Q3]), "depth" : 2.54 * mm});
        }
        {
            var Q0;
            Q0=makeQuery(id+"F0.imprint","IMPRINT",FACE,{"disambiguationData":[TD([[makeQuery(id+"F0.imprint","IMPRINT",EDGE,{"derivedFrom":sQuery(id+"F0.wireOp",EDGE,"E255")}),1.0]])]});
            extrude(context, id + "F5", {"entities" : qUnion([Q0]), "operationType" : NewBodyOperationType.ADD, "depth" : 10.16 * mm});
        }
        {
            var Q0;
            Q0=makeQuery(id+"F4.opExtrude","CAP_FACE",FACE,{"disambiguationData":[OSD([sQuery(id+"F0.wireOp",EDGE,"E0"),sQuery(id+"F0.wireOp",EDGE,"E1"),sQuery(id+"F0.wireOp",EDGE,"E2"),sQuery(id+"F0.wireOp",EDGE,"E3"),sQuery(id+"F0.wireOp",EDGE,"E4"),sQuery(id+"F0.wireOp",EDGE,"E8"),sQuery(id+"F0.wireOp",EDGE,"E12"),sQuery(id+"F0.wireOp",EDGE,"E16"),sQuery(id+"F0.wireOp",EDGE,"E17"),sQuery(id+"F0.wireOp",EDGE,"E18"),sQuery(id+"F0.wireOp",EDGE,"E19"),sQuery(id+"F0.wireOp",EDGE,"E20"),sQuery(id+"F0.wireOp",EDGE,"E21"),sQuery(id+"F0.wireOp",EDGE,"E22"),sQuery(id+"F0.wireOp",EDGE,"E23"),sQuery(id+"F0.wireOp",EDGE,"E24"),sQuery(id+"F0.wireOp",EDGE,"E31"),sQuery(id+"F0.wireOp",EDGE,"E32"),sQuery(id+"F0.wireOp",EDGE,"E33"),sQuery(id+"F0.wireOp",EDGE,"E34"),sQuery(id+"F0.wireOp",EDGE,"E35"),sQuery(id+"F0.wireOp",EDGE,"E36"),sQuery(id+"F0.wireOp",EDGE,"E37"),sQuery(id+"F0.wireOp",EDGE,"E38"),sQuery(id+"F0.wireOp",EDGE,"E39"),sQuery(id+"F0.wireOp",EDGE,"E40"),sQuery(id+"F0.wireOp",EDGE,"E41"),sQuery(id+"F0.wireOp",EDGE,"E42"),sQuery(id+"F0.wireOp",EDGE,"E43"),sQuery(id+"F0.wireOp",EDGE,"E44"),sQuery(id+"F0.wireOp",EDGE,"E45"),sQuery(id+"F0.wireOp",EDGE,"E46"),sQuery(id+"F0.wireOp",EDGE,"E47"),sQuery(id+"F0.wireOp",EDGE,"E48"),sQuery(id+"F0.wireOp",EDGE,"E49"),sQuery(id+"F0.wireOp",EDGE,"E50"),sQuery(id+"F0.wireOp",EDGE,"E51"),sQuery(id+"F0.wireOp",EDGE,"E52"),sQuery(id+"F0.wireOp",EDGE,"E53"),sQuery(id+"F0.wireOp",EDGE,"E54"),sQuery(id+"F0.wireOp",EDGE,"E55"),sQuery(id+"F0.wireOp",EDGE,"E56"),sQuery(id+"F0.wireOp",EDGE,"E57"),sQuery(id+"F0.wireOp",EDGE,"E58"),sQuery(id+"F0.wireOp",EDGE,"E59"),sQuery(id+"F0.wireOp",EDGE,"E61"),sQuery(id+"F0.wireOp",EDGE,"E62"),sQuery(id+"F0.wireOp",EDGE,"E63"),sQuery(id+"F0.wireOp",EDGE,"E113"),sQuery(id+"F0.wireOp",EDGE,"E114"),sQuery(id+"F0.wireOp",EDGE,"E115"),sQuery(id+"F0.wireOp",EDGE,"E116"),sQuery(id+"F0.wireOp",EDGE,"E117"),sQuery(id+"F0.wireOp",EDGE,"E118"),sQuery(id+"F0.wireOp",EDGE,"E119"),sQuery(id+"F0.wireOp",EDGE,"E120"),sQuery(id+"F0.wireOp",EDGE,"E121"),sQuery(id+"F0.wireOp",EDGE,"E122"),sQuery(id+"F0.wireOp",EDGE,"E123"),sQuery(id+"F0.wireOp",EDGE,"E124"),sQuery(id+"F0.wireOp",EDGE,"E126"),sQuery(id+"F0.wireOp",EDGE,"E127"),sQuery(id+"F0.wireOp",EDGE,"E128"),sQuery(id+"F0.wireOp",EDGE,"E129"),sQuery(id+"F0.wireOp",EDGE,"E130"),sQuery(id+"F0.wireOp",EDGE,"E131"),sQuery(id+"F0.wireOp",EDGE,"E132"),sQuery(id+"F0.wireOp",EDGE,"E133"),sQuery(id+"F0.wireOp",EDGE,"E134"),sQuery(id+"F0.wireOp",EDGE,"E135"),sQuery(id+"F0.wireOp",EDGE,"E136"),sQuery(id+"F0.wireOp",EDGE,"E137"),sQuery(id+"F0.wireOp",EDGE,"E138"),sQuery(id+"F0.wireOp",EDGE,"E139"),sQuery(id+"F0.wireOp",EDGE,"E140"),sQuery(id+"F0.wireOp",EDGE,"E141"),sQuery(id+"F0.wireOp",EDGE,"E142"),sQuery(id+"F0.wireOp",EDGE,"E143"),sQuery(id+"F0.wireOp",EDGE,"E144"),sQuery(id+"F0.wireOp",EDGE,"E145"),sQuery(id+"F0.wireOp",EDGE,"E146"),sQuery(id+"F0.wireOp",EDGE,"E147"),sQuery(id+"F0.wireOp",EDGE,"E158"),sQuery(id+"F0.wireOp",EDGE,"E159"),sQuery(id+"F0.wireOp",EDGE,"E160"),sQuery(id+"F0.wireOp",EDGE,"E161"),sQuery(id+"F0.wireOp",EDGE,"E162"),sQuery(id+"F0.wireOp",EDGE,"E163"),sQuery(id+"F0.wireOp",EDGE,"E164"),sQuery(id+"F0.wireOp",EDGE,"E165"),sQuery(id+"F0.wireOp",EDGE,"E166"),sQuery(id+"F0.wireOp",EDGE,"E167"),sQuery(id+"F0.wireOp",EDGE,"E168"),sQuery(id+"F0.wireOp",EDGE,"E169"),sQuery(id+"F0.wireOp",EDGE,"E170"),sQuery(id+"F0.wireOp",EDGE,"E171"),sQuery(id+"F0.wireOp",EDGE,"E172"),sQuery(id+"F0.wireOp",EDGE,"E173"),sQuery(id+"F0.wireOp",EDGE,"E174"),sQuery(id+"F0.wireOp",EDGE,"E175"),sQuery(id+"F0.wireOp",EDGE,"E176"),sQuery(id+"F0.wireOp",EDGE,"E177"),sQuery(id+"F0.wireOp",EDGE,"E178"),sQuery(id+"F0.wireOp",EDGE,"E179"),sQuery(id+"F0.wireOp",EDGE,"E180"),sQuery(id+"F0.wireOp",EDGE,"E181"),sQuery(id+"F0.wireOp",EDGE,"E182"),sQuery(id+"F0.wireOp",EDGE,"E183"),sQuery(id+"F0.wireOp",EDGE,"E184"),sQuery(id+"F0.wireOp",EDGE,"E185"),sQuery(id+"F0.wireOp",EDGE,"E186"),sQuery(id+"F0.wireOp",EDGE,"E187"),sQuery(id+"F0.wireOp",EDGE,"E188"),sQuery(id+"F0.wireOp",EDGE,"E189"),sQuery(id+"F0.wireOp",EDGE,"E190"),sQuery(id+"F0.wireOp",EDGE,"E191"),sQuery(id+"F0.wireOp",EDGE,"E192"),sQuery(id+"F0.wireOp",EDGE,"E193"),sQuery(id+"F0.wireOp",EDGE,"E194"),sQuery(id+"F0.wireOp",EDGE,"E195"),sQuery(id+"F0.wireOp",EDGE,"E196"),sQuery(id+"F0.wireOp",EDGE,"E197"),sQuery(id+"F0.wireOp",EDGE,"E198"),sQuery(id+"F0.wireOp",EDGE,"E199"),sQuery(id+"F0.wireOp",EDGE,"E200"),sQuery(id+"F0.wireOp",EDGE,"E201"),sQuery(id+"F0.wireOp",EDGE,"E202"),sQuery(id+"F0.wireOp",EDGE,"E203"),sQuery(id+"F0.wireOp",EDGE,"E204"),sQuery(id+"F0.wireOp",EDGE,"E205"),sQuery(id+"F0.wireOp",EDGE,"E206"),sQuery(id+"F0.wireOp",EDGE,"E207"),sQuery(id+"F0.wireOp",EDGE,"E208"),sQuery(id+"F0.wireOp",EDGE,"E209"),sQuery(id+"F0.wireOp",EDGE,"E210"),sQuery(id+"F0.wireOp",EDGE,"E211"),sQuery(id+"F0.wireOp",EDGE,"E212"),sQuery(id+"F0.wireOp",EDGE,"E213"),sQuery(id+"F0.wireOp",EDGE,"E214"),sQuery(id+"F0.wireOp",EDGE,"E219"),sQuery(id+"F0.wireOp",EDGE,"E220"),sQuery(id+"F0.wireOp",EDGE,"E221"),sQuery(id+"F0.wireOp",EDGE,"E222"),sQuery(id+"F0.wireOp",EDGE,"E223"),sQuery(id+"F0.wireOp",EDGE,"E224"),sQuery(id+"F0.wireOp",EDGE,"E225"),sQuery(id+"F0.wireOp",EDGE,"E226"),sQuery(id+"F0.wireOp",EDGE,"E228"),sQuery(id+"F0.wireOp",EDGE,"E229"),sQuery(id+"F0.wireOp",EDGE,"E230"),sQuery(id+"F0.wireOp",EDGE,"E232"),sQuery(id+"F0.wireOp",EDGE,"E233"),sQuery(id+"F0.wireOp",EDGE,"E234"),sQuery(id+"F0.wireOp",EDGE,"E235"),sQuery(id+"F0.wireOp",EDGE,"E236"),sQuery(id+"F0.wireOp",EDGE,"E237"),sQuery(id+"F0.wireOp",EDGE,"E238"),sQuery(id+"F0.wireOp",EDGE,"E239"),sQuery(id+"F0.wireOp",EDGE,"E240"),sQuery(id+"F0.wireOp",EDGE,"E241"),sQuery(id+"F0.wireOp",EDGE,"E242"),sQuery(id+"F0.wireOp",EDGE,"E243"),sQuery(id+"F0.wireOp",EDGE,"E244"),sQuery(id+"F0.wireOp",EDGE,"E245"),sQuery(id+"F0.wireOp",EDGE,"E246"),sQuery(id+"F0.wireOp",EDGE,"E247"),sQuery(id+"F0.wireOp",EDGE,"E248"),sQuery(id+"F0.wireOp",EDGE,"E249"),sQuery(id+"F0.wireOp",EDGE,"E250"),sQuery(id+"F0.wireOp",EDGE,"E251"),sQuery(id+"F0.wireOp",EDGE,"E252"),sQuery(id+"F0.wireOp",EDGE,"E253"),sQuery(id+"F0.wireOp",EDGE,"E254"),sQuery(id+"F0.wireOp",EDGE,"E255"),sQuery(id+"F0.wireOp",EDGE,"E256"),sQuery(id+"F0.wireOp",EDGE,"E257"),sQuery(id+"F0.wireOp",EDGE,"E258")])],"isStart":false});
            var sketch = newSketch(context, id + "F6", { "sketchPlane" : qUnion([Q0])});
            skLineSegment(sketch, "E297", {"start": v(66.75, 77.37) * mm, "end": v(67.78, 76.33) * mm});
            skLineSegment(sketch, "E298", {"start": v(67.78, 76.33) * mm, "end": v(46.56, 55.15) * mm});
            skLineSegment(sketch, "E299", {"start": v(46.56, 55.15) * mm, "end": v(46.56, 56.86) * mm});
            skLineSegment(sketch, "E300", {"start": v(46.56, 56.86) * mm, "end": v(66.75, 77.37) * mm});
            skSolve(sketch);
        }
        {
            var Q0;
            Q0=makeQuery(id+"F6.imprint","IMPRINT",FACE,{"disambiguationData":[TD([[makeQuery(id+"F6.imprint","IMPRINT",EDGE,{"derivedFrom":sQuery(id+"F6.wireOp",EDGE,"E297")}),-1.0]])]});
            extrude(context, id + "F7", {"entities" : qUnion([Q0]), "depth" : 38.1 * mm});
        }
    });
